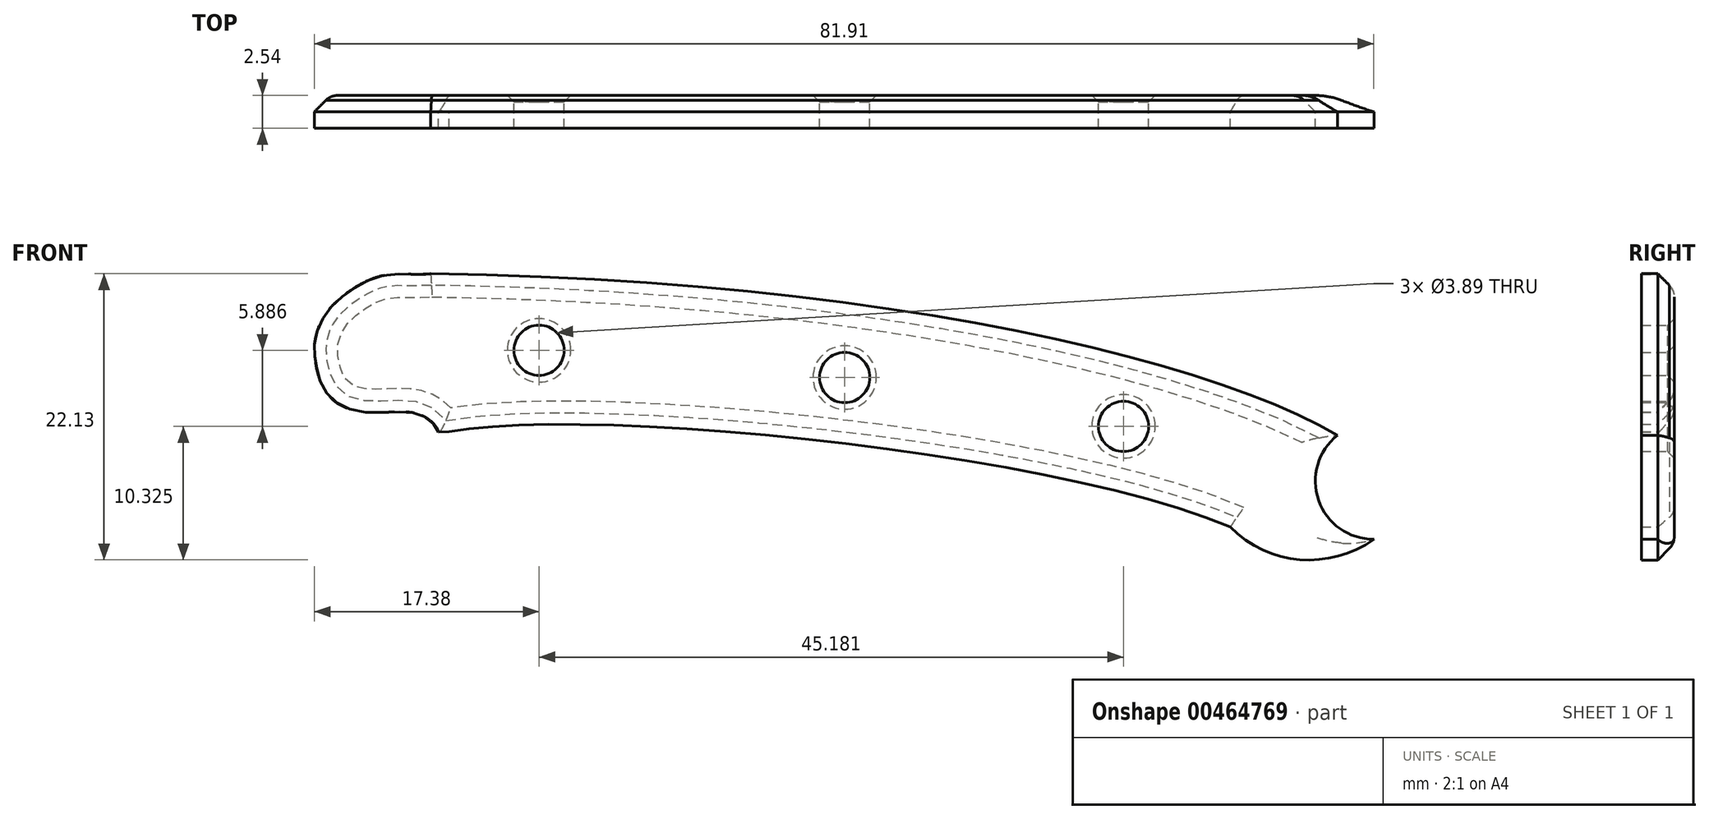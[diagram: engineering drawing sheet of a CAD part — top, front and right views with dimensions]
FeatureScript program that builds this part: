
annotation { "Feature Type Name" : "Feature", "Feature Type Description" : "" }
export const myFeature = defineFeature(function(context is Context, id is Id, definition is map)
    precondition{}
    {
        {
            var Q0;
            Q0=qCreatedBy(makeId("Front.planeOp"),FACE);
            var sketch = newSketch(context, id + "F0", { "sketchPlane" : qUnion([Q0])});
            skPoint(sketch, "E0", {"position": v(37.7, 34.47) * mm});
            skFitSpline(sketch, "E1", {"points": [v(7.11, 24.48) * mm, v(67.5, 17.12) * mm], "startDerivative": vector(32.5, 6.07) * mm, "endDerivative": vector(41.2, -17.48) * mm});
            skPoint(sketch, "E2", {"position": v(37.7, 23.57) * mm});
            skArc(sketch, "E3", {"start": v(67.5, 17.12) * mm, "mid": v(73.61, 14.57) * mm, "end": v(79.71, 17.12) * mm});
            skCircle(sketch, "E4", {"center": v(76.86, 19.24) * mm, "radius": 1.72 * mm});
            skCircle(sketch, "E5", {"center": v(14.07, 30.78) * mm, "radius": 1.94 * mm});
            skCircle(sketch, "E6", {"center": v(37.7, 28.68) * mm, "radius": 1.94 * mm});
            skCircle(sketch, "E7", {"center": v(59.25, 24.9) * mm, "radius": 1.94 * mm});
            skPoint(sketch, "E8", {"position": v(14.07, 36.48) * mm});
            skPoint(sketch, "E9", {"position": v(41.42, 33.95) * mm});
            skPoint(sketch, "E10", {"position": v(59.25, 30.4) * mm});
            skFitSpline(sketch, "E11", {"points": [v(5.7, 36.7) * mm, v(2.38, 36.62) * mm, v(-0.4, 35.48) * mm, v(-2.43, 33.6) * mm, v(-3.28, 31.36) * mm, v(-3.14, 29.43) * mm, v(-2.3, 27.4) * mm, v(0, 26.08) * mm, v(3.52, 26.03) * mm, v(5.36, 25.57) * mm, v(6.3, 24.46) * mm], "startDerivative": vector(-24.15, -3.51) * mm, "endDerivative": vector(1.15, -12.96) * mm});
            skFitSpline(sketch, "E12.trimOffspring", {"points": [v(-69.47, 27.87) * mm, v(79.71, 17.12) * mm], "startDerivative": vector(238.36, 61.55) * mm, "endDerivative": vector(-26.8, -33.68) * mm});
            skCircle(sketch, "E13", {"center": v(78.58, 20.67) * mm, "radius": 4.5 * mm});
            skLineSegment(sketch, "E14", {"start": v(7.11, 24.48) * mm, "end": v(6.3, 24.46) * mm});
            skSolve(sketch);
        }
        {
            var Q0;
            {var subQ1=sQuery(id+"F0.wireOp",EDGE,"E1");Q0=makeQuery(id+"F0.imprint","IMPRINT",FACE,{"disambiguationData":[TD([[makeQuery(id+"F0.imprint","IMPRINT",EDGE,{"derivedFrom":subQ1}),1.0]])]});}
            extrude(context, id + "F1", {"entities" : qUnion([Q0]), "depth" : 2.54 * mm});
        }
        {
            var Q0;
            Q0=makeQuery(id+"F1.opExtrude","CAP_EDGE",EDGE,{"disambiguationData":[OSD([sQuery(id+"F0.wireOp",EDGE,"E12.trimOffspring")])],"isStart":true});
            var Q1;
            Q1=makeQuery(id+"F1.opExtrude","CAP_EDGE",EDGE,{"disambiguationData":[OSD([sQuery(id+"F0.wireOp",EDGE,"E1")])],"isStart":true});
            var Q2;
            Q2=makeQuery(id+"F1.opExtrude","CAP_EDGE",EDGE,{"disambiguationData":[OSD([sQuery(id+"F0.wireOp",EDGE,"E3")])],"isStart":true});
            var Q3;
            Q3=makeQuery(id+"F1.opExtrude","CAP_EDGE",EDGE,{"disambiguationData":[OSD([sQuery(id+"F0.wireOp",EDGE,"E13")])],"isStart":true});
            var Q4;
            Q4=makeQuery(id+"F1.opExtrude","CAP_EDGE",EDGE,{"disambiguationData":[OSD([sQuery(id+"F0.wireOp",EDGE,"E11")])],"isStart":true});
            var Q5;
            Q5=makeQuery(id+"F1.opExtrude","CAP_EDGE",EDGE,{"disambiguationData":[OSD([sQuery(id+"F0.wireOp",EDGE,"E14")])],"isStart":true});
            chamfer(context, id + "F2", {"entities" : qUnion([Q0, Q1, Q2, Q3, Q4, Q5]), "width" : 1.27 * mm, "tangentPropagation" : true});
        }
        {
            var Q0;
            {var subQ0=sQuery(id+"F0.wireOp",EDGE,"E12.trimOffspring");Q0=makeQuery(id+"F2.opChamfer","BLEND_EDGE",EDGE,{"blendedFrom":[makeQuery(id+"F1.opExtrude","CAP_EDGE",EDGE,{"disambiguationData":[OSD([subQ0])],"isStart":true}),makeQuery(id+"F1.opExtrude","CAP_FACE",FACE,{"disambiguationData":[OSD([sQuery(id+"F0.wireOp",EDGE,"E1"),sQuery(id+"F0.wireOp",EDGE,"E3"),sQuery(id+"F0.wireOp",EDGE,"E5"),sQuery(id+"F0.wireOp",EDGE,"E6"),sQuery(id+"F0.wireOp",EDGE,"E7"),sQuery(id+"F0.wireOp",EDGE,"E11"),subQ0,sQuery(id+"F0.wireOp",EDGE,"E13"),sQuery(id+"F0.wireOp",EDGE,"E14")])],"isStart":true})],"blendedInto":[makeQuery(id+"F1.opExtrude","CAP_FACE",FACE,{"disambiguationData":[OSD([sQuery(id+"F0.wireOp",EDGE,"E1"),sQuery(id+"F0.wireOp",EDGE,"E3"),sQuery(id+"F0.wireOp",EDGE,"E5"),sQuery(id+"F0.wireOp",EDGE,"E6"),sQuery(id+"F0.wireOp",EDGE,"E7"),sQuery(id+"F0.wireOp",EDGE,"E11"),subQ0,sQuery(id+"F0.wireOp",EDGE,"E13"),sQuery(id+"F0.wireOp",EDGE,"E14")])],"isStart":true})]});}
            var Q1;
            {var subQ0=sQuery(id+"F0.wireOp",EDGE,"E1");Q1=makeQuery(id+"F2.opChamfer","BLEND_EDGE",EDGE,{"blendedFrom":[makeQuery(id+"F1.opExtrude","CAP_EDGE",EDGE,{"disambiguationData":[OSD([subQ0])],"isStart":true}),makeQuery(id+"F1.opExtrude","CAP_FACE",FACE,{"disambiguationData":[OSD([subQ0,sQuery(id+"F0.wireOp",EDGE,"E3"),sQuery(id+"F0.wireOp",EDGE,"E5"),sQuery(id+"F0.wireOp",EDGE,"E6"),sQuery(id+"F0.wireOp",EDGE,"E7"),sQuery(id+"F0.wireOp",EDGE,"E11"),sQuery(id+"F0.wireOp",EDGE,"E12.trimOffspring"),sQuery(id+"F0.wireOp",EDGE,"E13"),sQuery(id+"F0.wireOp",EDGE,"E14")])],"isStart":true})],"blendedInto":[makeQuery(id+"F1.opExtrude","CAP_FACE",FACE,{"disambiguationData":[OSD([subQ0,sQuery(id+"F0.wireOp",EDGE,"E3"),sQuery(id+"F0.wireOp",EDGE,"E5"),sQuery(id+"F0.wireOp",EDGE,"E6"),sQuery(id+"F0.wireOp",EDGE,"E7"),sQuery(id+"F0.wireOp",EDGE,"E11"),sQuery(id+"F0.wireOp",EDGE,"E12.trimOffspring"),sQuery(id+"F0.wireOp",EDGE,"E13"),sQuery(id+"F0.wireOp",EDGE,"E14")])],"isStart":true})]});}
            var Q2;
            {var subQ0=sQuery(id+"F0.wireOp",EDGE,"E13");Q2=makeQuery(id+"F2.opChamfer","BLEND_EDGE",EDGE,{"blendedFrom":[makeQuery(id+"F1.opExtrude","CAP_EDGE",EDGE,{"disambiguationData":[OSD([subQ0])],"isStart":true}),makeQuery(id+"F1.opExtrude","CAP_FACE",FACE,{"disambiguationData":[OSD([sQuery(id+"F0.wireOp",EDGE,"E1"),sQuery(id+"F0.wireOp",EDGE,"E3"),sQuery(id+"F0.wireOp",EDGE,"E5"),sQuery(id+"F0.wireOp",EDGE,"E6"),sQuery(id+"F0.wireOp",EDGE,"E7"),sQuery(id+"F0.wireOp",EDGE,"E11"),sQuery(id+"F0.wireOp",EDGE,"E12.trimOffspring"),subQ0,sQuery(id+"F0.wireOp",EDGE,"E14")])],"isStart":true})],"blendedInto":[makeQuery(id+"F1.opExtrude","CAP_FACE",FACE,{"disambiguationData":[OSD([sQuery(id+"F0.wireOp",EDGE,"E1"),sQuery(id+"F0.wireOp",EDGE,"E3"),sQuery(id+"F0.wireOp",EDGE,"E5"),sQuery(id+"F0.wireOp",EDGE,"E6"),sQuery(id+"F0.wireOp",EDGE,"E7"),sQuery(id+"F0.wireOp",EDGE,"E11"),sQuery(id+"F0.wireOp",EDGE,"E12.trimOffspring"),subQ0,sQuery(id+"F0.wireOp",EDGE,"E14")])],"isStart":true})]});}
            var Q3;
            {var subQ0=sQuery(id+"F0.wireOp",EDGE,"E11");Q3=makeQuery(id+"F2.opChamfer","BLEND_EDGE",EDGE,{"blendedFrom":[makeQuery(id+"F1.opExtrude","CAP_EDGE",EDGE,{"disambiguationData":[OSD([subQ0])],"isStart":true}),makeQuery(id+"F1.opExtrude","CAP_FACE",FACE,{"disambiguationData":[OSD([sQuery(id+"F0.wireOp",EDGE,"E1"),sQuery(id+"F0.wireOp",EDGE,"E3"),sQuery(id+"F0.wireOp",EDGE,"E5"),sQuery(id+"F0.wireOp",EDGE,"E6"),sQuery(id+"F0.wireOp",EDGE,"E7"),subQ0,sQuery(id+"F0.wireOp",EDGE,"E12.trimOffspring"),sQuery(id+"F0.wireOp",EDGE,"E13"),sQuery(id+"F0.wireOp",EDGE,"E14")])],"isStart":true})],"blendedInto":[makeQuery(id+"F1.opExtrude","CAP_FACE",FACE,{"disambiguationData":[OSD([sQuery(id+"F0.wireOp",EDGE,"E1"),sQuery(id+"F0.wireOp",EDGE,"E3"),sQuery(id+"F0.wireOp",EDGE,"E5"),sQuery(id+"F0.wireOp",EDGE,"E6"),sQuery(id+"F0.wireOp",EDGE,"E7"),subQ0,sQuery(id+"F0.wireOp",EDGE,"E12.trimOffspring"),sQuery(id+"F0.wireOp",EDGE,"E13"),sQuery(id+"F0.wireOp",EDGE,"E14")])],"isStart":true})]});}
            var Q4;
            {var subQ0=sQuery(id+"F0.wireOp",EDGE,"E3");Q4=makeQuery(id+"F2.opChamfer","BLEND_EDGE",EDGE,{"blendedFrom":[makeQuery(id+"F1.opExtrude","CAP_EDGE",EDGE,{"disambiguationData":[OSD([subQ0])],"isStart":true}),makeQuery(id+"F1.opExtrude","CAP_FACE",FACE,{"disambiguationData":[OSD([sQuery(id+"F0.wireOp",EDGE,"E1"),subQ0,sQuery(id+"F0.wireOp",EDGE,"E5"),sQuery(id+"F0.wireOp",EDGE,"E6"),sQuery(id+"F0.wireOp",EDGE,"E7"),sQuery(id+"F0.wireOp",EDGE,"E11"),sQuery(id+"F0.wireOp",EDGE,"E12.trimOffspring"),sQuery(id+"F0.wireOp",EDGE,"E13"),sQuery(id+"F0.wireOp",EDGE,"E14")])],"isStart":true})],"blendedInto":[makeQuery(id+"F1.opExtrude","CAP_FACE",FACE,{"disambiguationData":[OSD([sQuery(id+"F0.wireOp",EDGE,"E1"),subQ0,sQuery(id+"F0.wireOp",EDGE,"E5"),sQuery(id+"F0.wireOp",EDGE,"E6"),sQuery(id+"F0.wireOp",EDGE,"E7"),sQuery(id+"F0.wireOp",EDGE,"E11"),sQuery(id+"F0.wireOp",EDGE,"E12.trimOffspring"),sQuery(id+"F0.wireOp",EDGE,"E13"),sQuery(id+"F0.wireOp",EDGE,"E14")])],"isStart":true})]});}
            fillet(context, id + "F3", {"entities" : qUnion([Q0, Q1, Q2, Q3, Q4]), "radius" : 1.27 * mm, "allowEdgeOverflow" : false});
        }
        {
            var Q0;
            Q0=makeQuery(id+"F1.opExtrude","CAP_EDGE",EDGE,{"disambiguationData":[OSD([sQuery(id+"F0.wireOp",EDGE,"E7")])],"isStart":true});
            var Q1;
            Q1=makeQuery(id+"F1.opExtrude","CAP_EDGE",EDGE,{"disambiguationData":[OSD([sQuery(id+"F0.wireOp",EDGE,"E6")])],"isStart":true});
            var Q2;
            Q2=makeQuery(id+"F1.opExtrude","CAP_EDGE",EDGE,{"disambiguationData":[OSD([sQuery(id+"F0.wireOp",EDGE,"E5")])],"isStart":true});
            chamfer(context, id + "F4", {"entities" : qUnion([Q0, Q1, Q2]), "width" : 0.5 * mm, "tangentPropagation" : true});
        }
    });
